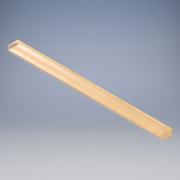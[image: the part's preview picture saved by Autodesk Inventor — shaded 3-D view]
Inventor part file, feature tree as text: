
AUTODESK INVENTOR PART (.ipt)
format: ipt  version: 2022.2 (Build 262287010, 287A)  size: 183,808 bytes
history: native  units: in
note: dims shown in document units (in); Inventor stores cm internally (conversion verified against a paired STEP export)
features: revolve x2, direct_edit x1, extrude x1, sketch x1, projected_geometry x1
ambient origin geometry x8: Origin, YZ Plane, XZ Plane, XY Plane, X Axis, Y Axis, Z Axis, Center Point
bodies: Solid1 (feature_tree), Body1 (feature_tree)
feature tree (6):
  direct_edit  "Direct Edit1"
  extrude  "Extrusion1"  [1 undecoded]
  sketch  "Sketch1"  dims[d0=180.0deg d1=-0.6184in d2=0.375in d3=0.0in]
  projected_geometry  "Projected Loop1"
  revolve  "Rotate1"  [1 undecoded]
  revolve  "Rotate2"  [1 undecoded]
note: 3 required parameter values undecoded (feature->parameter linkage not recoverable at this tier; creation-order binding heuristic only, values carry confidence <= 0.55)